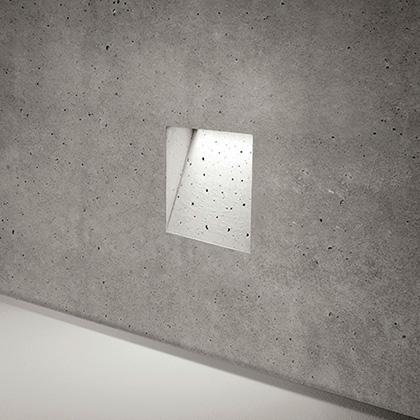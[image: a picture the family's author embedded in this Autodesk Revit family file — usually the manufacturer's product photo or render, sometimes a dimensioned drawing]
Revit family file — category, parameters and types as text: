
# Revit family: SIMES_C.8028W_Ghost
name_source: partatom
category: Lighting Fixtures
revit_build: Autodesk Revit 2016 (Build: 20150714_1515(x64)
units: mm (PartAtom-declared; Revit-internal decimal feet)

## family parameters
Cut with Voids When Loaded = No
Host = Face
Light Source = Yes
Part Type = Normal
Room Calculation Point = No
Round Connector Dimension = Use Diameter
Shared = No

## types (1)
- SIMES_C.8028W_Ghost
    Approval mark = CE
    Assembly Code = D5020
    Color Filter = 16777215
    Color Rendering Index = CRI 80
    Colour Temperature = 3000
    Control Gear = electronic transformer
    Default Elevation = 1219 mm
    Description = MINIGHOST SQUARE
Art. C.8028W
MODULES LED 3000K  230V CRI 80
Rated luminaire luminous flux: 268lm
Rated input power: 6W
Luminaire efficacy: 45lm/W
Electronic ballast 220÷230V 50-60Hz
CE

PRODUCT TYPE
Wall mounted luminaire. IP rating IP 65
MATERIAL CHARACTERISTICS
Ghost is a lighting void that is obtained from a polypropylene housing anchored to the retaining panels before pouring the concrete. Ghost is composed of two elements: the housing and the lighting element. The housing is in polypropylene and it consists of two complementary parts: - A jig , which forms the housing, and is extracted together with the retaining panel after completing the casting and removing the anchor screws; - The housing  that remains embedded inside the casting and houses the lighting element. (The housing is supplied with bolts, locking system and stickers to be applied on the outside of the retaining panels so to secure a perfect alignment for multiple installations of each housing when pouring the concrete). The lighting element in die cast aluminum is anchored to the casing  through proper screws and it remains completely hided into the void. Mechanical resistance IK 06
MAINTENANCE
This product is manufactured on site during the concrete casting of the wall with hand crafted procedures; therefore, small imperfections caused by the low accurance of the casting, subsidence of the concrete surface, actual and future cracks, colour ripples and variations over time, will be deliberately present and they are a feature of the concrete, proving the hand-made manufacturing procedure.
LIGHTING PERFORMANCE
Toughened glass diffuser. LOR -- 
WIRING
Supplied with a pre-wired 0.3m H05RN-F cable. Isolation: CLASS I . Available colours: Cast cement. Weight:  Kg Glow Wire test: --
L.E.D circuit included.
GHOST PATENDED, REGISTERED DESIGN
This luminaire contains built-in LED modules with energy class: A, A+, A++. In case of damage or malfunction please contact the manufacturer to receive additional instructions on how to replace and relative spare parts to order. The LED modules cannot be handled in the luminaire by the end user (Regulation UE 874/2012).
LED circuit boards are engineered accordingly to actual Lumen Maintenance regulation (LM80) and Technical Memorandum (TM21) where uniformity and quality of light is 50.000 hours referred to L70  B20 Ta 25°C.Lifecycle refers to LED circuit boards only, all others components of the luminaire are excluded.
    Dimming Lamp Color Temperature Shift = <None>
    Frequency = 50-60Hz
    IFC Classification = Light Fixture
    IK Rating = IK 06
    Lamp = LED
    Lamp Light Flux = 490
    Lamp count = 1
    Last Update = 02/08/2018 10:21:42
    Lifetime = 50000 L70 B20 Ta 25°C
    Light Output Ratio = 100
    Luminous efficacy = 44,7
    Manufacturer = SIMES
    Masterformat 2014 Code = 26 56 00
    Masterformat 2014 Description = Exterior Lighting
    Model = C.8028W
    Mounting Place = Wall
    Mounting Type = Recessed
    NBS Reference Code = 49
    NBS Reference Description = Luminaries And Lamps
    OmniClass Code = 23-35 47 11
    OmniClass Description = Lighting Fixture
    Photometric Web File = C8028W.ies
    Product Group = recessed luminaire
    Product Name = Ghost for cast concrete
    Protection Class = Protection class I
    Protection Degree = IP 65
    System Light Flux = 268
    System Power = 6
    Tilt Angle = 0.00°
    Type Comments = SIMES S.p.A. - All rights reserved
    Type Image = minighost-quadrato.jpg
    UNSPSC Code = 3911
    URL = http://www.simes.it
    Uniclass 1.4 Code = YJ73
    Uniclass 1.4 Description = Luminaries and lamps
    Uniclass 2.0 Code = PR-49
    Uniclass 2.0 Description = Luminaries and lamps
    Uniclass 2015 Code = EF_70_80
    Uniclass 2015 Name = Lighting
    Uniformat II Code = D5020
    Uniformat II Description = Lighting & Branch Wiring
    Voltage = 220÷230V
    Wattage Comments = 18.0W
